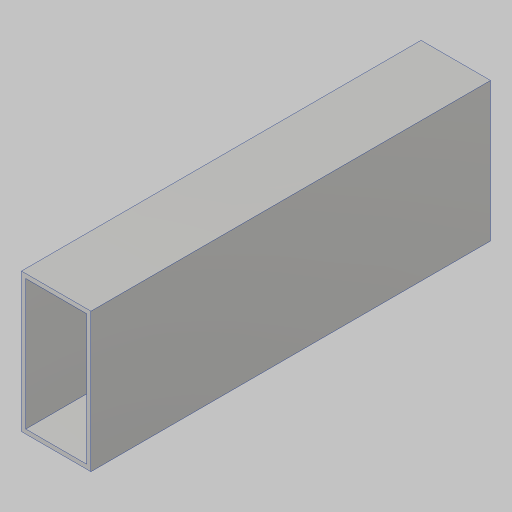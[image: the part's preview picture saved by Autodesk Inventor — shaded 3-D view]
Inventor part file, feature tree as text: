
AUTODESK INVENTOR PART (.ipt)
format: ipt  version: 2023.5 (Build 275446000, 446)  size: 100,864 bytes
history: native  units: in
note: dims shown in document units (in); Inventor stores cm internally (conversion verified against a paired STEP export)
features: extrude x1
ambient origin geometry x8: Origin, YZ Plane, XZ Plane, XY Plane, X Axis, Y Axis, Z Axis, Center Point
bodies: Solid1 (feature_tree)
feature tree (1):
  extrude  "Extrusion1"  TaperAngle=0.0deg  [1 undecoded]
note: 1 required parameter value undecoded (feature->parameter linkage not recoverable at this tier; creation-order binding heuristic only, values carry confidence <= 0.55)
